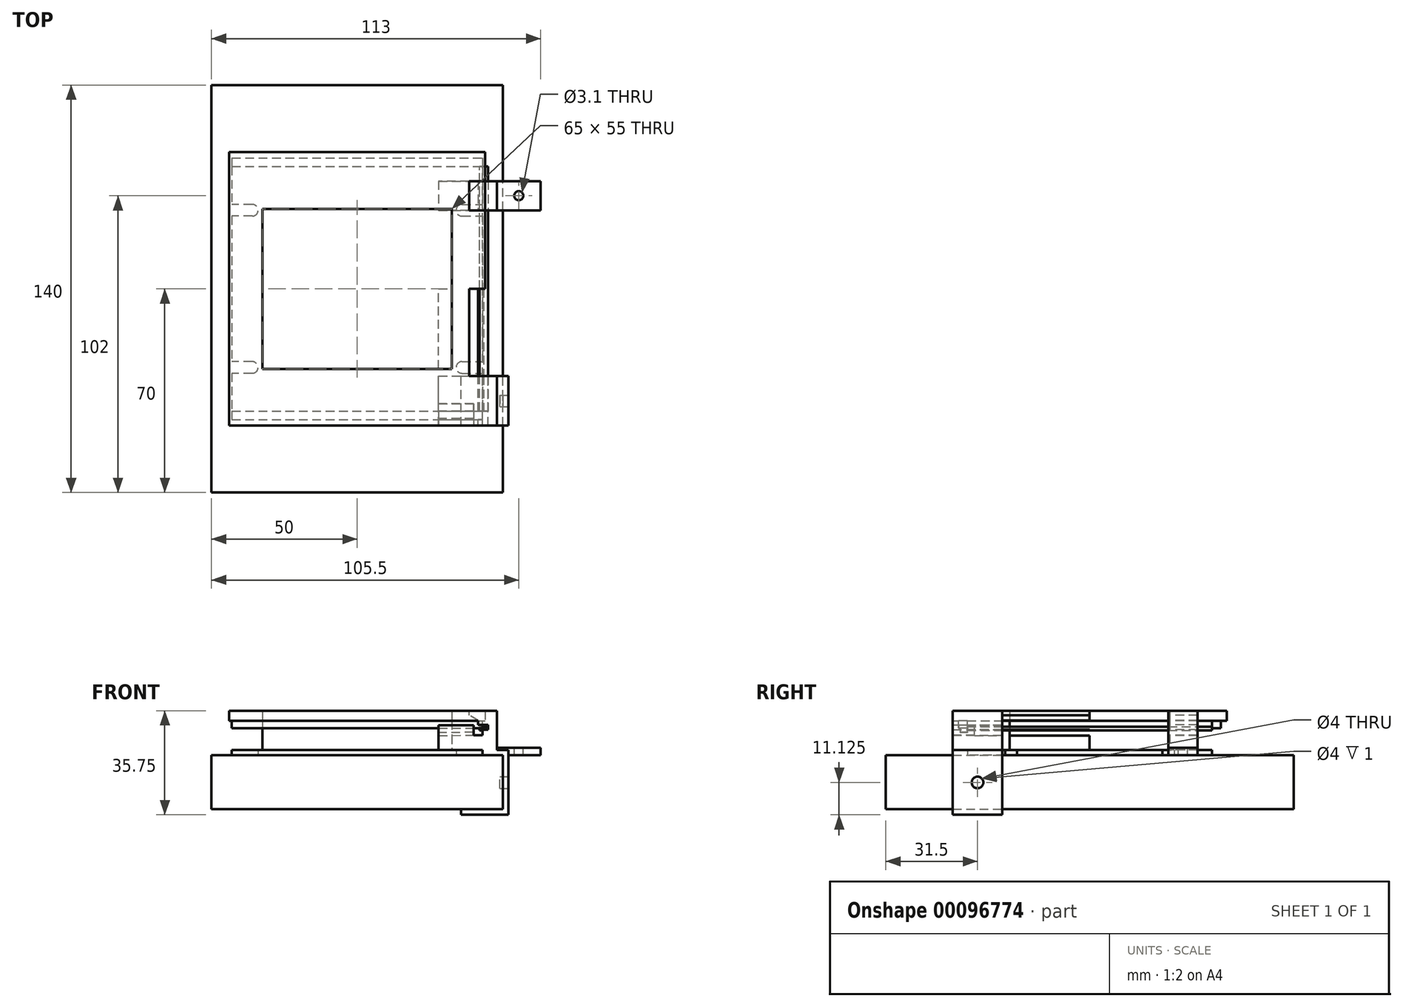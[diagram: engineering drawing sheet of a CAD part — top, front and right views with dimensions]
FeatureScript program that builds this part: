
annotation { "Feature Type Name" : "Feature", "Feature Type Description" : "" }
export const myFeature = defineFeature(function(context is Context, id is Id, definition is map)
    precondition{}
    {
        {
            var Q0;
            Q0=qCreatedBy(makeId("Top.planeOp"),FACE);
            var sketch = newSketch(context, id + "F0", { "sketchPlane" : qUnion([Q0])});
            skLineSegment(sketch, "E0.bottom", {"start": v(-50, -70) * mm, "end": v(50, -70) * mm});
            skLineSegment(sketch, "E0.top", {"start": v(-50, 70) * mm, "end": v(50, 70) * mm});
            skLineSegment(sketch, "E0.left", {"start": v(-50, -70) * mm, "end": v(-50, 70) * mm});
            skLineSegment(sketch, "E0.right", {"start": v(50, -70) * mm, "end": v(50, 70) * mm});
            skPoint(sketch, "E0.middle", {"position": v(0, 0) * mm});
            skSolve(sketch);
        }
        {
            var Q0;
            Q0=qSketchRegion(id+"F0",true);
            extrude(context, id + "F1", {"entities" : qUnion([Q0]), "oppositeDirection" : true, "depth" : 18.5 * mm});
        }
        {
            var Q0;
            Q0=qCreatedBy(makeId("Top.planeOp"),FACE);
            var sketch = newSketch(context, id + "F2", { "sketchPlane" : qUnion([Q0])});
            skLineSegment(sketch, "E1.bottom", {"start": v(-43, 42) * mm, "end": v(43, 42) * mm});
            skLineSegment(sketch, "E1.top", {"start": v(-43, -42) * mm, "end": v(43, -42) * mm});
            skLineSegment(sketch, "E1.left", {"start": v(-43, 42) * mm, "end": v(-43, 29) * mm});
            skLineSegment(sketch, "E1.right", {"start": v(43, 42) * mm, "end": v(43, 29) * mm});
            skPoint(sketch, "E1.middle", {"position": v(0, 0) * mm});
            skArc(sketch, "E2", {"start": v(-36, 25) * mm, "mid": v(-34, 27) * mm, "end": v(-36, 29) * mm});
            skLineSegment(sketch, "E3", {"start": v(-36, 25) * mm, "end": v(-43, 25) * mm});
            skLineSegment(sketch, "E4", {"start": v(-36, 29) * mm, "end": v(-43, 29) * mm});
            skArc(sketch, "E5.MirrorCS", {"start": v(36, 25) * mm, "mid": v(34, 27) * mm, "end": v(36, 29) * mm});
            skLineSegment(sketch, "E6.MirrorCS", {"start": v(36, 29) * mm, "end": v(43, 29) * mm});
            skLineSegment(sketch, "E7.MirrorCS", {"start": v(36, 25) * mm, "end": v(43, 25) * mm});
            skLineSegment(sketch, "E8.MirrorCS", {"start": v(-36, -25) * mm, "end": v(-43, -25) * mm});
            skLineSegment(sketch, "E9.MirrorCS", {"start": v(-36, -29) * mm, "end": v(-43, -29) * mm});
            skArc(sketch, "E10.MirrorCS", {"start": v(-36, -25) * mm, "mid": v(-34, -27) * mm, "end": v(-36, -29) * mm});
            skLineSegment(sketch, "E11.MirrorCS", {"start": v(36, -25) * mm, "end": v(43, -25) * mm});
            skLineSegment(sketch, "E12.MirrorCS", {"start": v(36, -29) * mm, "end": v(43, -29) * mm});
            skArc(sketch, "E13.MirrorCS", {"start": v(36, -25) * mm, "mid": v(34, -27) * mm, "end": v(36, -29) * mm});
            skLineSegment(sketch, "E14.trimOffspring", {"start": v(-43, 25) * mm, "end": v(-43, -25) * mm});
            skLineSegment(sketch, "E15.trimOffspring", {"start": v(-43, -29) * mm, "end": v(-43, -42) * mm});
            skLineSegment(sketch, "E16.trimOffspring", {"start": v(43, -29) * mm, "end": v(43, -42) * mm});
            skLineSegment(sketch, "E17.trimOffspring", {"start": v(43, 25) * mm, "end": v(43, -25) * mm});
            skSolve(sketch);
        }
        {
            var Q0;
            Q0=qSketchRegion(id+"F2",true);
            extrude(context, id + "F3", {"entities" : qUnion([Q0]), "depth" : 1.75 * mm});
        }
        {
            var Q0;
            Q0=makeQuery(id+"F3.opExtrude","CAP_FACE",FACE,{"disambiguationData":[OSD([sQuery(id+"F2.wireOp",EDGE,"E1.bottom"),sQuery(id+"F2.wireOp",EDGE,"E1.top"),sQuery(id+"F2.wireOp",EDGE,"E1.left"),sQuery(id+"F2.wireOp",EDGE,"E1.right"),sQuery(id+"F2.wireOp",EDGE,"E2"),sQuery(id+"F2.wireOp",EDGE,"E3"),sQuery(id+"F2.wireOp",EDGE,"E4"),sQuery(id+"F2.wireOp",EDGE,"E5.MirrorCS"),sQuery(id+"F2.wireOp",EDGE,"E6.MirrorCS"),sQuery(id+"F2.wireOp",EDGE,"E7.MirrorCS"),sQuery(id+"F2.wireOp",EDGE,"E8.MirrorCS"),sQuery(id+"F2.wireOp",EDGE,"E9.MirrorCS"),sQuery(id+"F2.wireOp",EDGE,"E10.MirrorCS"),sQuery(id+"F2.wireOp",EDGE,"E11.MirrorCS"),sQuery(id+"F2.wireOp",EDGE,"E12.MirrorCS"),sQuery(id+"F2.wireOp",EDGE,"E13.MirrorCS"),sQuery(id+"F2.wireOp",EDGE,"E14.trimOffspring"),sQuery(id+"F2.wireOp",EDGE,"E15.trimOffspring"),sQuery(id+"F2.wireOp",EDGE,"E16.trimOffspring"),sQuery(id+"F2.wireOp",EDGE,"E17.trimOffspring")])],"isStart":false});
            var sketch = newSketch(context, id + "F4", { "sketchPlane" : qUnion([Q0])});
            skLineSegment(sketch, "E18.bottom", {"start": v(-45, 47) * mm, "end": v(45, 47) * mm});
            skLineSegment(sketch, "E18.top", {"start": v(-45, -47) * mm, "end": v(45, -47) * mm});
            skLineSegment(sketch, "E18.left", {"start": v(-45, 47) * mm, "end": v(-45, -47) * mm});
            skLineSegment(sketch, "E18.right", {"start": v(45, 47) * mm, "end": v(45, -47) * mm});
            skPoint(sketch, "E18.middle", {"position": v(0, 0) * mm});
            skLineSegment(sketch, "E19.bottom", {"start": v(-43, 45) * mm, "end": v(43, 45) * mm});
            skLineSegment(sketch, "E19.top", {"start": v(-43, -45) * mm, "end": v(43, -45) * mm});
            skLineSegment(sketch, "E19.left", {"start": v(-43, 45) * mm, "end": v(-43, -45) * mm});
            skLineSegment(sketch, "E19.right", {"start": v(43, 45) * mm, "end": v(43, -45) * mm});
            skLineSegment(sketch, "E20", {"start": v(-43, 45) * mm, "end": v(-45, 45) * mm});
            skLineSegment(sketch, "E21", {"start": v(43, 45) * mm, "end": v(45, 45) * mm});
            skLineSegment(sketch, "E22.MirrorCS", {"start": v(-43, -45) * mm, "end": v(-45, -45) * mm});
            skLineSegment(sketch, "E23.MirrorCS", {"start": v(43, -45) * mm, "end": v(45, -45) * mm});
            skLineSegment(sketch, "E24", {"start": v(-43, 45) * mm, "end": v(-43, 47) * mm});
            skLineSegment(sketch, "E25.MirrorCS", {"start": v(43, 45) * mm, "end": v(43, 47) * mm});
            skLineSegment(sketch, "E26.MirrorCS", {"start": v(-43, -45) * mm, "end": v(-43, -47) * mm});
            skLineSegment(sketch, "E27.MirrorCS", {"start": v(43, -45) * mm, "end": v(43, -47) * mm});
            skLineSegment(sketch, "E28.bottom", {"start": v(-32.5, 27.5) * mm, "end": v(32.5, 27.5) * mm});
            skLineSegment(sketch, "E28.top", {"start": v(-32.5, -27.5) * mm, "end": v(32.5, -27.5) * mm});
            skLineSegment(sketch, "E28.left", {"start": v(-32.5, 27.5) * mm, "end": v(-32.5, -27.5) * mm});
            skLineSegment(sketch, "E28.right", {"start": v(32.5, 27.5) * mm, "end": v(32.5, -27.5) * mm});
            skSolve(sketch);
        }
        {
            var Q0;
            Q0=makeQuery(id+"F4.imprint","IMPRINT",FACE,{"disambiguationData":[TD([[makeQuery(id+"F4.imprint","IMPRINT",EDGE,{"derivedFrom":sQuery(id+"F4.wireOp",EDGE,"E28.bottom")}),-1.0]])]});
            extrude(context, id + "F5", {"entities" : qUnion([Q0]), "depth" : 10 * mm});
        }
        {
            var Q0;
            Q0=makeQuery(id+"F5.opExtrude","CAP_FACE",FACE,{"disambiguationData":[OSD([sQuery(id+"F4.wireOp",EDGE,"E28.bottom"),sQuery(id+"F4.wireOp",EDGE,"E28.top"),sQuery(id+"F4.wireOp",EDGE,"E28.left"),sQuery(id+"F4.wireOp",EDGE,"E28.right")])],"isStart":false});
            var sketch = newSketch(context, id + "F6", { "sketchPlane" : qUnion([Q0])});
            skLineSegment(sketch, "E29.bottom", {"start": v(-44, 47) * mm, "end": v(44, 47) * mm});
            skLineSegment(sketch, "E29.top", {"start": v(-44, -47) * mm, "end": v(44, -47) * mm});
            skLineSegment(sketch, "E29.left", {"start": v(-44, 47) * mm, "end": v(-44, -47) * mm});
            skLineSegment(sketch, "E29.right", {"start": v(44, 47) * mm, "end": v(44, -47) * mm});
            skPoint(sketch, "E29.middle", {"position": v(0, 0) * mm});
            skLineSegment(sketch, "E30.bottom", {"start": v(-43, 45) * mm, "end": v(43, 45) * mm});
            skLineSegment(sketch, "E30.top", {"start": v(-43, -45) * mm, "end": v(43, -45) * mm});
            skLineSegment(sketch, "E30.left", {"start": v(-43, 45) * mm, "end": v(-43, -45) * mm});
            skLineSegment(sketch, "E30.right", {"start": v(43, 45) * mm, "end": v(43, -45) * mm});
            skLineSegment(sketch, "E31.MirrorCS", {"start": v(-43, -44) * mm, "end": v(-43, -45) * mm});
            skLineSegment(sketch, "E32.MirrorCS", {"start": v(43, -44) * mm, "end": v(43, -45) * mm});
            skLineSegment(sketch, "E33.bottom", {"start": v(-32.5, 27.5) * mm, "end": v(32.5, 27.5) * mm});
            skLineSegment(sketch, "E33.top", {"start": v(-32.5, -27.5) * mm, "end": v(32.5, -27.5) * mm});
            skLineSegment(sketch, "E33.left", {"start": v(-32.5, 27.5) * mm, "end": v(-32.5, -27.5) * mm});
            skLineSegment(sketch, "E33.right", {"start": v(32.5, 27.5) * mm, "end": v(32.5, -27.5) * mm});
            skLineSegment(sketch, "E34.0", {"start": v(-43, 42) * mm, "end": v(43, 42) * mm});
            skLineSegment(sketch, "E35.0", {"start": v(-43, -42) * mm, "end": v(43, -42) * mm});
            skSolve(sketch);
        }
        {
            var Q0;
            Q0=makeQuery(id+"F6.imprint","IMPRINT",FACE,{"disambiguationData":[TD([[makeQuery(id+"F6.imprint","IMPRINT",EDGE,{"derivedFrom":sQuery(id+"F6.wireOp",EDGE,"E30.bottom")}),1.0]])]});
            var Q1;
            {var subQ0=sQuery(id+"F6.wireOp",EDGE,"E30.bottom");Q1=makeQuery(id+"F6.imprint","IMPRINT",FACE,{"disambiguationData":[TD([[makeQuery(id+"F6.imprint","IMPRINT",EDGE,{"derivedFrom":subQ0}),-1.0]])]});}
            var Q2;
            Q2=makeQuery(id+"F6.imprint","IMPRINT",FACE,{"disambiguationData":[TD([[makeQuery(id+"F6.imprint","IMPRINT",EDGE,{"derivedFrom":sQuery(id+"F6.wireOp",EDGE,"E33.bottom")}),1.0]])]});
            var Q3;
            {var subQ0=sQuery(id+"F6.wireOp",EDGE,"E30.top");Q3=makeQuery(id+"F6.imprint","IMPRINT",FACE,{"disambiguationData":[TD([[makeQuery(id+"F6.imprint","IMPRINT",EDGE,{"derivedFrom":subQ0}),1.0]])]});}
            var Q4;
            Q4=makeQuery(id+"F6.imprint","IMPRINT",FACE,{"disambiguationData":[TD([[makeQuery(id+"F6.imprint","IMPRINT",EDGE,{"derivedFrom":sQuery(id+"F6.wireOp",EDGE,"E30.top")}),-1.0]])]});
            extrude(context, id + "F7", {"entities" : qUnion([Q0, Q1, Q2, Q3, Q4]), "depth" : 3.5 * mm});
        }
        {
            var Q0;
            {var subQ0=sQuery(id+"F6.wireOp",EDGE,"E30.bottom");Q0=makeQuery(id+"F6.imprint","IMPRINT",FACE,{"disambiguationData":[TD([[makeQuery(id+"F6.imprint","IMPRINT",EDGE,{"derivedFrom":subQ0}),-1.0]])]});}
            var Q1;
            {var subQ0=sQuery(id+"F6.wireOp",EDGE,"E30.top");Q1=makeQuery(id+"F6.imprint","IMPRINT",FACE,{"disambiguationData":[TD([[makeQuery(id+"F6.imprint","IMPRINT",EDGE,{"derivedFrom":subQ0}),1.0]])]});}
            extrude(context, id + "F8", {"entities" : qUnion([Q0, Q1]), "operationType" : NewBodyOperationType.ADD, "oppositeDirection" : true, "depth" : 2.5 * mm});
        }
        {
            var Q0;
            Q0=qCreatedBy(makeId("Front.planeOp"),FACE);
            var sketch = newSketch(context, id + "F9", { "sketchPlane" : qUnion([Q0])});
            skLineSegment(sketch, "E36.0", {"start": v(43, 13.75) * mm, "end": v(43, 10.25) * mm});
            skLineSegment(sketch, "E37.0", {"start": v(43, 13.75) * mm, "end": v(43, 9.75) * mm});
            skLineSegment(sketch, "E38.0", {"start": v(43, 7.25) * mm, "end": v(43, 9.75) * mm});
            skLineSegment(sketch, "E39", {"start": v(43, 9.75) * mm, "end": v(43, 8.5) * mm});
            skLineSegment(sketch, "E40", {"start": v(43, 8.5) * mm, "end": v(45, 9.75) * mm});
            skLineSegment(sketch, "E41", {"start": v(45, 9.75) * mm, "end": v(43, 9.75) * mm});
            skLineSegment(sketch, "E42.bottom", {"start": v(43, 9.75) * mm, "end": v(42, 9.75) * mm});
            skLineSegment(sketch, "E42.top", {"start": v(43, 8.5) * mm, "end": v(42, 8.5) * mm});
            skLineSegment(sketch, "E42.right", {"start": v(42, 9.75) * mm, "end": v(42, 8.5) * mm});
            skSolve(sketch);
        }
        {
            var Q0;
            Q0=qSketchRegion(id+"F9",true);
            extrude(context, id + "F10", {"entities" : qUnion([Q0]), "operationType" : NewBodyOperationType.ADD, "depth" : 42 * mm, "hasSecondDirection" : true, "secondDirectionOppositeDirection" : true, "secondDirectionDepth" : 42 * mm});
        }
        {
            var Q0;
            Q0=qCreatedBy(makeId("Front.planeOp"),FACE);
            var sketch = newSketch(context, id + "F11", { "sketchPlane" : qUnion([Q0])});
            skLineSegment(sketch, "E43.0", {"start": v(28, 1.75) * mm, "end": v(43, 1.75) * mm});
            skLineSegment(sketch, "E44.0", {"start": v(43, 1.75) * mm, "end": v(43, 0) * mm});
            skLineSegment(sketch, "E45", {"start": v(43, 0) * mm, "end": v(48, 0) * mm});
            skPoint(sketch, "E46.orphan", {"position": v(43, 9.75) * mm});
            skPoint(sketch, "E47.orphan", {"position": v(-43, 9.25) * mm});
            skPoint(sketch, "E48.orphan", {"position": v(-43, 1.75) * mm});
            skPoint(sketch, "E49.end.orphan", {"position": v(43, 7.25) * mm});
            skLineSegment(sketch, "E50", {"start": v(27.97, 6.75) * mm, "end": v(28, 1.75) * mm});
            skLineSegment(sketch, "E51", {"start": v(48, 13.75) * mm, "end": v(48, 1.75) * mm});
            skPoint(sketch, "E52.0.end.orphan", {"position": v(45, 9.75) * mm});
            skLineSegment(sketch, "E53.0", {"start": v(45, 9.75) * mm, "end": v(43, 9.75) * mm, "construction": true});
            skLineSegment(sketch, "E54.0", {"start": v(43, 8.5) * mm, "end": v(45, 9.75) * mm, "construction": true});
            skLineSegment(sketch, "E55", {"start": v(27.97, 6.75) * mm, "end": v(43, 6.84) * mm});
            skLineSegment(sketch, "E56.bottom", {"start": v(43, 0) * mm, "end": v(52, 0) * mm});
            skLineSegment(sketch, "E56.top", {"start": v(48, 1.75) * mm, "end": v(52, 1.75) * mm});
            skLineSegment(sketch, "E56.left", {"start": v(43, 0) * mm, "end": v(43, 1.75) * mm});
            skLineSegment(sketch, "E57.right", {"start": v(41.5, 11.88) * mm, "end": v(41.5, 10.45) * mm});
            skLineSegment(sketch, "E58", {"start": v(38.5, 13.75) * mm, "end": v(41.5, 11.88) * mm});
            skLineSegment(sketch, "E59", {"start": v(41.5, 10.45) * mm, "end": v(44.97, 10.45) * mm});
            skLineSegment(sketch, "E60", {"start": v(44.97, 10.45) * mm, "end": v(45, 8.79) * mm});
            skLineSegment(sketch, "E61", {"start": v(45, 8.79) * mm, "end": v(43, 8.75) * mm});
            skPoint(sketch, "E62.orphan", {"position": v(43, 10) * mm});
            skPoint(sketch, "E63.orphan", {"position": v(41.5, 10) * mm});
            skLineSegment(sketch, "E64", {"start": v(43, 8.75) * mm, "end": v(43, 6.84) * mm});
            skLineSegment(sketch, "E65.top", {"start": v(38.5, 15.25) * mm, "end": v(48, 15.25) * mm});
            skLineSegment(sketch, "E65.left", {"start": v(38.5, 13.75) * mm, "end": v(38.5, 15.25) * mm});
            skLineSegment(sketch, "E65.right", {"start": v(48, 13.75) * mm, "end": v(48, 15.25) * mm});
            skPoint(sketch, "E57.bottom.end.orphan", {"position": v(41.5, 13.75) * mm});
            skLineSegment(sketch, "E66.0", {"start": v(50, -18.5) * mm, "end": v(50, 0) * mm});
            skLineSegment(sketch, "E67.0", {"start": v(-50, -18.5) * mm, "end": v(50, -18.5) * mm});
            skLineSegment(sketch, "E68", {"start": v(48, 0) * mm, "end": v(50, 0) * mm});
            skLineSegment(sketch, "E69", {"start": v(50, -18.5) * mm, "end": v(35.7, -18.5) * mm});
            skLineSegment(sketch, "E70", {"start": v(35.7, -18.5) * mm, "end": v(35.7, -20.5) * mm});
            skLineSegment(sketch, "E71", {"start": v(35.7, -20.5) * mm, "end": v(52, -20.5) * mm});
            skLineSegment(sketch, "E72", {"start": v(52, -20.5) * mm, "end": v(52, 1.75) * mm});
            skPoint(sketch, "E56.right.end.orphan", {"position": v(63, 1.75) * mm});
            skSolve(sketch);
        }
        {
            var Q0;
            Q0=qSketchRegion(id+"F11",true);
            extrude(context, id + "F12", {"entities" : qUnion([Q0]), "depth" : 47 * mm});
        }
        {
            var Q0;
            Q0=qSketchRegion(id+"F11",true);
            extrude(context, id + "F13", {"entities" : qUnion([Q0]), "operationType" : NewBodyOperationType.REMOVE, "depth" : 30 * mm});
        }
        {
            var Q0;
            Q0=makeQuery(id+"F12.opExtrude","SWEPT_FACE",FACE,{"disambiguationData":[OSD([sQuery(id+"F11.wireOp",EDGE,"E50")])]});
            var sketch = newSketch(context, id + "F14", { "sketchPlane" : qUnion([Q0])});
            skPoint(sketch, "E73.right.end.orphan", {"position": v(-45, -81.5) * mm});
            skPoint(sketch, "E74.0.end.orphan", {"position": v(42, 12) * mm});
            skPoint(sketch, "E74.0.start.orphan", {"position": v(-42, 9.5) * mm});
            skPoint(sketch, "E75.0.end.orphan", {"position": v(-45, 12) * mm});
            skPoint(sketch, "E75.0.start.orphan", {"position": v(-45, 9.5) * mm});
            skPoint(sketch, "E76.0.end.orphan", {"position": v(-45, 9.08) * mm});
            skPoint(sketch, "E76.0.start.orphan", {"position": v(42, 7.08) * mm});
            skPoint(sketch, "E77.0.3.end.orphan", {"position": v(47, 6.58) * mm});
            skPoint(sketch, "E77.0.3.start.orphan", {"position": v(47, 6.58) * mm});
            skPoint(sketch, "E77.0.1.end.orphan", {"position": v(30, 6.58) * mm});
            skPoint(sketch, "E77.0.1.start.orphan", {"position": v(30, 6.58) * mm});
            skLineSegment(sketch, "E78.0", {"start": v(-45, 9.5) * mm, "end": v(-45, 12) * mm, "construction": true});
            skLineSegment(sketch, "E79.0", {"start": v(42, 8.25) * mm, "end": v(42, 9.58) * mm, "construction": true});
            skLineSegment(sketch, "E80.0", {"start": v(-45, 12) * mm, "end": v(-46, 12) * mm, "construction": true});
            skLineSegment(sketch, "E81.0", {"start": v(-45, 12) * mm, "end": v(-135, 12) * mm, "construction": true});
            skLineSegment(sketch, "E82.top", {"start": v(47, 5.94) * mm, "end": v(39.5, 5.94) * mm});
            skPoint(sketch, "E83.orphan", {"position": v(39.5, 7.08) * mm});
            skLineSegment(sketch, "E84", {"start": v(-45, 11.58) * mm, "end": v(-45, 9.08) * mm});
            skLineSegment(sketch, "E85", {"start": v(47, 10.08) * mm, "end": v(47, 5.94) * mm});
            skPoint(sketch, "E86.orphan", {"position": v(-42, 8.25) * mm});
            skLineSegment(sketch, "E87.right", {"start": v(47, 10.08) * mm, "end": v(47, 7.08) * mm});
            skPoint(sketch, "E88.orphan", {"position": v(45, 12) * mm});
            skPoint(sketch, "E89.0.start.orphan", {"position": v(45, 9.5) * mm});
            skLineSegment(sketch, "E90", {"start": v(44.5, 10.08) * mm, "end": v(44.5, 7.58) * mm});
            skLineSegment(sketch, "E91", {"start": v(42, 7.58) * mm, "end": v(42, 9.58) * mm});
            skLineSegment(sketch, "E92", {"start": v(39.5, 9.58) * mm, "end": v(39.5, 5.94) * mm});
            skLineSegment(sketch, "E93", {"start": v(42, 7.58) * mm, "end": v(44.5, 7.58) * mm});
            skLineSegment(sketch, "E94.top", {"start": v(42, 10.08) * mm, "end": v(39.5, 10.08) * mm});
            skLineSegment(sketch, "E94.left", {"start": v(42, 9.58) * mm, "end": v(42, 10.08) * mm});
            skLineSegment(sketch, "E94.right", {"start": v(39.5, 9.58) * mm, "end": v(39.5, 10.08) * mm});
            skLineSegment(sketch, "E95", {"start": v(44.5, 10.08) * mm, "end": v(47, 10.08) * mm});
            skSolve(sketch);
        }
        {
            var Q0;
            Q0=qSketchRegion(id+"F14",true);
            extrude(context, id + "F15", {"entities" : qUnion([Q0]), "operationType" : NewBodyOperationType.ADD, "oppositeDirection" : true, "depth" : 12 * mm});
        }
        {
            var Q0;
            Q0=makeQuery(id+"F12.opExtrude","SWEPT_FACE",FACE,{"disambiguationData":[OSD([sQuery(id+"F11.wireOp",EDGE,"E72")])]});
            var sketch = newSketch(context, id + "F16", { "sketchPlane" : qUnion([Q0])});
            skCircle(sketch, "E96", {"center": v(-38.5, -9.38) * mm, "radius": 2 * mm});
            skPoint(sketch, "E96.centerSnap0", {"position": v(-47, -9.38) * mm});
            skPoint(sketch, "E96.centerSnap1", {"position": v(-38.5, 1.75) * mm});
            skSolve(sketch);
        }
        {
            var Q0;
            Q0=qSketchRegion(id+"F16",true);
            extrude(context, id + "F17", {"entities" : qUnion([Q0]), "operationType" : NewBodyOperationType.REMOVE, "oppositeDirection" : true, "depth" : 3 * mm});
        }
        {
            var Q0;
            Q0=makeQuery(id+"F13.boolean.opBoolean","COPY",FACE,{"derivedFrom":makeQuery(id+"F13.opExtrude","CAP_FACE",FACE,{"disambiguationData":[OSD([sQuery(id+"F11.wireOp",EDGE,"E43.0"),sQuery(id+"F11.wireOp",EDGE,"E50"),sQuery(id+"F11.wireOp",EDGE,"E51"),sQuery(id+"F11.wireOp",EDGE,"E55"),sQuery(id+"F11.wireOp",EDGE,"E56.bottom"),sQuery(id+"F11.wireOp",EDGE,"E56.top"),sQuery(id+"F11.wireOp",EDGE,"E56.left"),sQuery(id+"F11.wireOp",EDGE,"E57.right"),sQuery(id+"F11.wireOp",EDGE,"E58"),sQuery(id+"F11.wireOp",EDGE,"E59"),sQuery(id+"F11.wireOp",EDGE,"E60"),sQuery(id+"F11.wireOp",EDGE,"E61"),sQuery(id+"F11.wireOp",EDGE,"E64"),sQuery(id+"F11.wireOp",EDGE,"E65.top"),sQuery(id+"F11.wireOp",EDGE,"E65.left"),sQuery(id+"F11.wireOp",EDGE,"E65.right"),sQuery(id+"F11.wireOp",EDGE,"E66.0"),sQuery(id+"F11.wireOp",EDGE,"E68"),sQuery(id+"F11.wireOp",EDGE,"E69"),sQuery(id+"F11.wireOp",EDGE,"E70"),sQuery(id+"F11.wireOp",EDGE,"E71"),sQuery(id+"F11.wireOp",EDGE,"E72")])],"isStart":false})});
            cPlane(context, id + "F18", {"entities" : qUnion([Q0]), "cplaneType" : CPlaneType.OFFSET, "offset" : 57 * mm, "width" : 150 * mm, "height" : 150 * mm});
        }
        {
            var Q0;
            Q0=qCreatedBy(id+"F18.planeOp",FACE);
            var sketch = newSketch(context, id + "F19", { "sketchPlane" : qUnion([Q0])});
            skLineSegment(sketch, "E97.0.0", {"start": v(-28, 1.75) * mm, "end": v(-27.97, 6.75) * mm});
            skLineSegment(sketch, "E97.0.1", {"start": v(-27.97, 6.75) * mm, "end": v(-43, 6.84) * mm});
            skLineSegment(sketch, "E97.0.2", {"start": v(-43, 6.84) * mm, "end": v(-43, 8.75) * mm});
            skLineSegment(sketch, "E97.0.3", {"start": v(-43, 8.75) * mm, "end": v(-45, 8.79) * mm});
            skLineSegment(sketch, "E97.0.4", {"start": v(-45, 8.79) * mm, "end": v(-44.97, 10.45) * mm});
            skLineSegment(sketch, "E97.0.5", {"start": v(-44.97, 10.45) * mm, "end": v(-41.5, 10.45) * mm});
            skLineSegment(sketch, "E97.0.6", {"start": v(-41.5, 10.45) * mm, "end": v(-41.5, 11.88) * mm});
            skLineSegment(sketch, "E97.0.7", {"start": v(-41.5, 11.88) * mm, "end": v(-38.5, 13.75) * mm});
            skLineSegment(sketch, "E97.0.8", {"start": v(-38.5, 13.75) * mm, "end": v(-38.5, 15.25) * mm});
            skLineSegment(sketch, "E97.0.9", {"start": v(-38.5, 15.25) * mm, "end": v(-48, 15.25) * mm});
            skLineSegment(sketch, "E97.0.10", {"start": v(-48, 15.25) * mm, "end": v(-48, 2.5) * mm});
            skLineSegment(sketch, "E97.0.18", {"start": v(-43, 0) * mm, "end": v(-43, 1.75) * mm});
            skLineSegment(sketch, "E97.0.19", {"start": v(-43, 1.75) * mm, "end": v(-28, 1.75) * mm});
            skPoint(sketch, "E97.0.16.end.orphan", {"position": v(-50, 0) * mm});
            skPoint(sketch, "E97.0.15.end.orphan", {"position": v(-50, -18.5) * mm});
            skPoint(sketch, "E97.0.13.start.orphan", {"position": v(-52, -20.5) * mm});
            skPoint(sketch, "E97.0.14.end.orphan", {"position": v(-35.7, -18.5) * mm});
            skPoint(sketch, "E97.0.14.start.orphan", {"position": v(-35.7, -20.5) * mm});
            skLineSegment(sketch, "E98.bottom", {"start": v(-43, 0) * mm, "end": v(-63, 0) * mm});
            skLineSegment(sketch, "E98.top", {"start": v(-48, 2.5) * mm, "end": v(-63, 2.5) * mm});
            skLineSegment(sketch, "E98.right", {"start": v(-63, 0) * mm, "end": v(-63, 2.5) * mm});
            skPoint(sketch, "E97.0.11.end.orphan", {"position": v(-52, 1.75) * mm});
            skPoint(sketch, "E99.orphan", {"position": v(-48, 1.75) * mm});
            skLineSegment(sketch, "E100.0", {"start": v(-39.97, 6.82) * mm, "end": v(-39.95, 10.32) * mm, "construction": true});
            skSolve(sketch);
        }
        {
            var Q0;
            Q0=qSketchRegion(id+"F19",true);
            extrude(context, id + "F20", {"entities" : qUnion([Q0]), "depth" : 10 * mm});
        }
        {
            var Q0;
            Q0=makeQuery(id+"F20.opExtrude","SWEPT_FACE",FACE,{"disambiguationData":[OSD([sQuery(id+"F19.wireOp",EDGE,"E98.top")])]});
            var sketch = newSketch(context, id + "F21", { "sketchPlane" : qUnion([Q0])});
            skLineSegment(sketch, "E101.0.0", {"start": v(48, 27) * mm, "end": v(63, 27) * mm, "construction": true});
            skLineSegment(sketch, "E101.0.1", {"start": v(63, 27) * mm, "end": v(63, 37) * mm, "construction": true});
            skLineSegment(sketch, "E101.0.2", {"start": v(63, 37) * mm, "end": v(48, 37) * mm, "construction": true});
            skLineSegment(sketch, "E101.0.3", {"start": v(48, 37) * mm, "end": v(48, 27) * mm, "construction": true});
            skPoint(sketch, "E102", {"position": v(55.5, 32) * mm});
            skPoint(sketch, "E102.positionSnap0", {"position": v(63, 32) * mm});
            skPoint(sketch, "E102.positionSnap1", {"position": v(55.5, 27) * mm});
            skCircle(sketch, "E103", {"center": v(55.5, 32) * mm, "radius": 1.55 * mm});
            skSolve(sketch);
        }
        {
            var Q0;
            Q0=qSketchRegion(id+"F21",true);
            extrude(context, id + "F22", {"entities" : qUnion([Q0]), "operationType" : NewBodyOperationType.REMOVE, "oppositeDirection" : true, "depth" : 25 * mm});
        }
    });
